# Revit family: E929-1.9
name_source: partatom
category: Plumbing Fixtures
revit_build: Autodesk Revit 2015 (Build: 20140223_1515(x64)
units: mm (PartAtom-declared; Revit-internal decimal feet)

## types (1)
- E929-1.9
    Accesorios = Conectores ½ -14 NPSM
    Características del Producto = Monomando de lavabo sin contra, cuadrado inclinado.
    Cuerpo de Latón = Brass
    Default Elevation = 35"
    Description = Monomando de lavabo sin contra, cuadrado inclinado.
    Garantía = El producto HELVEX está garantizado como libre de defectos en materiales y procesos de fabricación. El producto HELVEX está garantizado, en lo que se refiere a los acabados; por un periodo de 10 años en los acabados cromo y duravex, y por 2 años en acabados diferentes al cromo, a partir de la fecha de compra indicada en la factura
    Instalación = Conexión ½ - 14 NPSM
    Manufacturer = HELVEX S.A. de C.V.
    Model = E-929
    Operación = El maneral tienen una rotación horizontal para la función de agua caliente y fría; y vertical para abrir y cerrar el flujo de agua.
    Presión Máxima de Trabajo = 85.3 psi
    Presión Mínima de Trabajo = 3.6 psi
    Total Depth = 6"
    Total Height = 6"
    Total Width = 1"
    Type Comments = Monomando de Lavabo con Contra

## geometry (parser evidence)
native form markers: Sweep x3
no freeform markers — native parametric forms only
